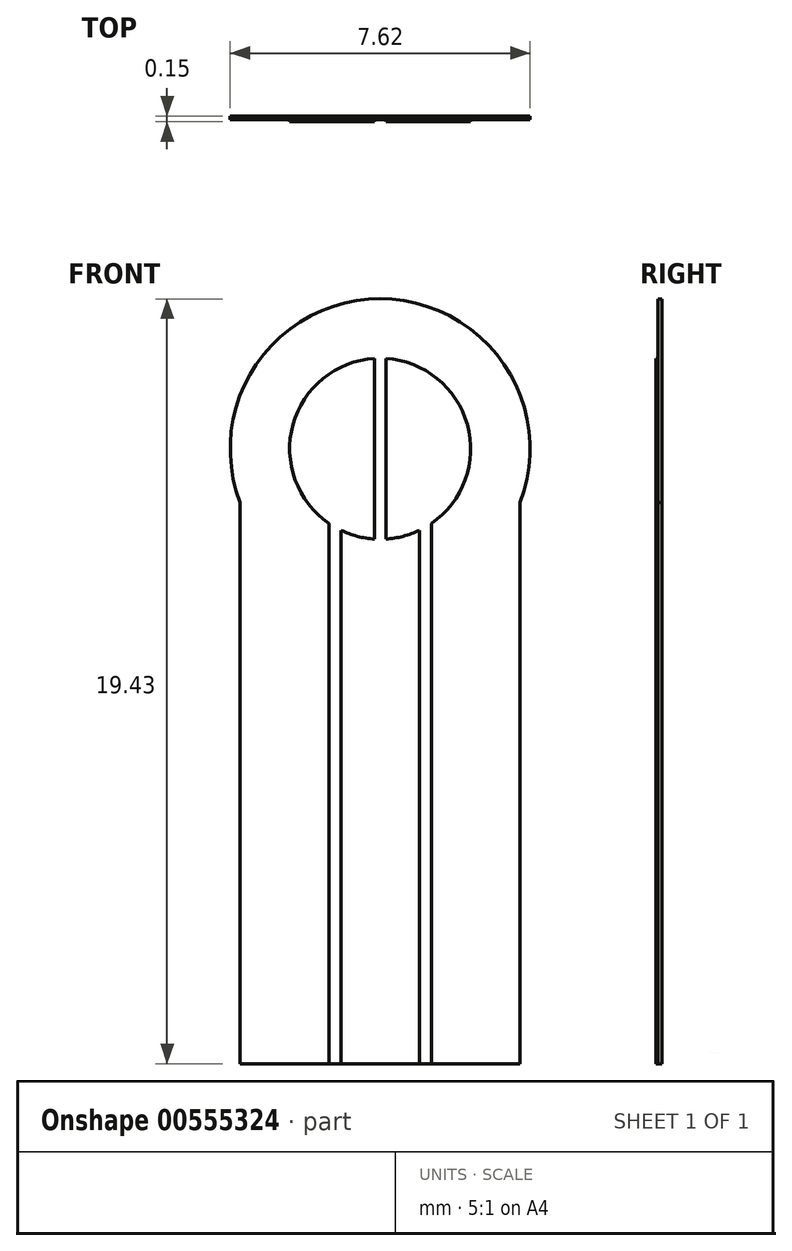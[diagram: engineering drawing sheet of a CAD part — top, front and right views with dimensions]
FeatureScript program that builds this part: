
annotation { "Feature Type Name" : "Feature", "Feature Type Description" : "" }
export const myFeature = defineFeature(function(context is Context, id is Id, definition is map)
    precondition{}
    {
        {
            var Q0;
            Q0=qCreatedBy(makeId("Front.planeOp"),FACE);
            var sketch = newSketch(context, id + "F0", { "sketchPlane" : qUnion([Q0])});
            skLineSegment(sketch, "E0.bottom", {"start": v(3.56, -7.81) * mm, "end": v(-3.56, -7.81) * mm});
            skLineSegment(sketch, "E0.left", {"start": v(3.56, -7.81) * mm, "end": v(3.56, 6.44) * mm});
            skLineSegment(sketch, "E0.right", {"start": v(-3.56, -7.81) * mm, "end": v(-3.56, 6.44) * mm});
            skPoint(sketch, "E0.middle", {"position": v(0, 0) * mm});
            skArc(sketch, "E1", {"start": v(3.56, 6.44) * mm, "mid": v(0, 11.62) * mm, "end": v(-3.56, 6.44) * mm});
            skPoint(sketch, "E2.orphan", {"position": v(-3.56, 7.81) * mm});
            skPoint(sketch, "E3.orphan", {"position": v(3.56, 7.81) * mm});
            skSolve(sketch);
        }
        {
            var Q0;
            Q0 = qSketchRegion(id + "F0", true);
            extrude(context, id + "F1", {"entities" : qUnion([Q0]), "depth" : 0.1 * mm, "offsetDistance" : 25 * mm});
        }
        {
            var Q0;
            Q0=makeQuery(id+"F1.opExtrude","CAP_FACE",FACE,{"disambiguationData":[OSD([sQuery(id+"F0.wireOp",EDGE,"E0.bottom"),sQuery(id+"F0.wireOp",EDGE,"E0.left"),sQuery(id+"F0.wireOp",EDGE,"E0.right"),sQuery(id+"F0.wireOp",EDGE,"E1")])],"isStart":false});
            var sketch = newSketch(context, id + "F2", { "sketchPlane" : qUnion([Q0])});
            skArc(sketch, "E4", {"start": v(-0.14, 10.1) * mm, "mid": v(-2.22, 8.42) * mm, "end": v(-1.3, 5.92) * mm});
            skLineSegment(sketch, "E5.left", {"start": v(0.14, 10.1) * mm, "end": v(0.14, 5.52) * mm});
            skLineSegment(sketch, "E5.right", {"start": v(-0.14, 10.1) * mm, "end": v(-0.14, 5.52) * mm});
            skPoint(sketch, "E6.orphan", {"position": v(-0.14, 10.61) * mm});
            skPoint(sketch, "E7.orphan", {"position": v(0.14, 10.61) * mm});
            skArc(sketch, "E8.trimOffspring", {"start": v(0.14, 5.52) * mm, "mid": v(0.58, 5.59) * mm, "end": v(1, 5.74) * mm});
            skPoint(sketch, "E9.orphan", {"position": v(-0.14, 5.01) * mm});
            skPoint(sketch, "E10.orphan", {"position": v(0.14, 5.01) * mm});
            skLineSegment(sketch, "E11", {"start": v(0, 7.81) * mm, "end": v(-2.3, 7.81) * mm, "construction": true});
            skLineSegment(sketch, "E12", {"start": v(0, 7.81) * mm, "end": v(2.3, 7.81) * mm, "construction": true});
            skLineSegment(sketch, "E13", {"start": v(-1.15, 5.82) * mm, "end": v(-1.15, -7.81) * mm, "construction": true});
            skLineSegment(sketch, "E14", {"start": v(1.15, 5.82) * mm, "end": v(1.15, -7.81) * mm, "construction": true});
            skLineSegment(sketch, "E15.bottom", {"start": v(-1.3, 7.81) * mm, "end": v(-1, 7.81) * mm});
            skLineSegment(sketch, "E15.top", {"start": v(-1.3, -7.81) * mm, "end": v(-1, -7.81) * mm});
            skLineSegment(sketch, "E15.left", {"start": v(-1.3, 5.92) * mm, "end": v(-1.3, -7.81) * mm});
            skLineSegment(sketch, "E15.right", {"start": v(-1, 5.74) * mm, "end": v(-1, -7.81) * mm});
            skPoint(sketch, "E15.middle", {"position": v(-1.15, 0) * mm});
            skLineSegment(sketch, "E16.bottom", {"start": v(1, 7.81) * mm, "end": v(1.3, 7.81) * mm});
            skLineSegment(sketch, "E16.top", {"start": v(1, -7.81) * mm, "end": v(1.3, -7.81) * mm});
            skLineSegment(sketch, "E16.left", {"start": v(1, 5.74) * mm, "end": v(1, -7.81) * mm});
            skLineSegment(sketch, "E16.right", {"start": v(1.3, 5.92) * mm, "end": v(1.3, -7.81) * mm});
            skPoint(sketch, "E16.middle", {"position": v(1.15, 0) * mm});
            skPoint(sketch, "E17.orphan", {"position": v(-1.15, 7.81) * mm});
            skArc(sketch, "E18.trimOffspring", {"start": v(-1, 5.74) * mm, "mid": v(-0.58, 5.59) * mm, "end": v(-0.14, 5.52) * mm});
            skPoint(sketch, "E19.orphan", {"position": v(1.15, 7.81) * mm});
            skArc(sketch, "E20.trimOffspring", {"start": v(1.3, 5.92) * mm, "mid": v(2.22, 8.42) * mm, "end": v(0.14, 10.1) * mm});
            skSolve(sketch);
        }
        {
            var Q0;
            Q0 = qSketchRegion(id + "F2", true);
            extrude(context, id + "F3", {"entities" : qUnion([Q0]), "operationType" : NewBodyOperationType.ADD, "depth" : 0.05 * mm, "offsetDistance" : 25 * mm});
        }
    });
